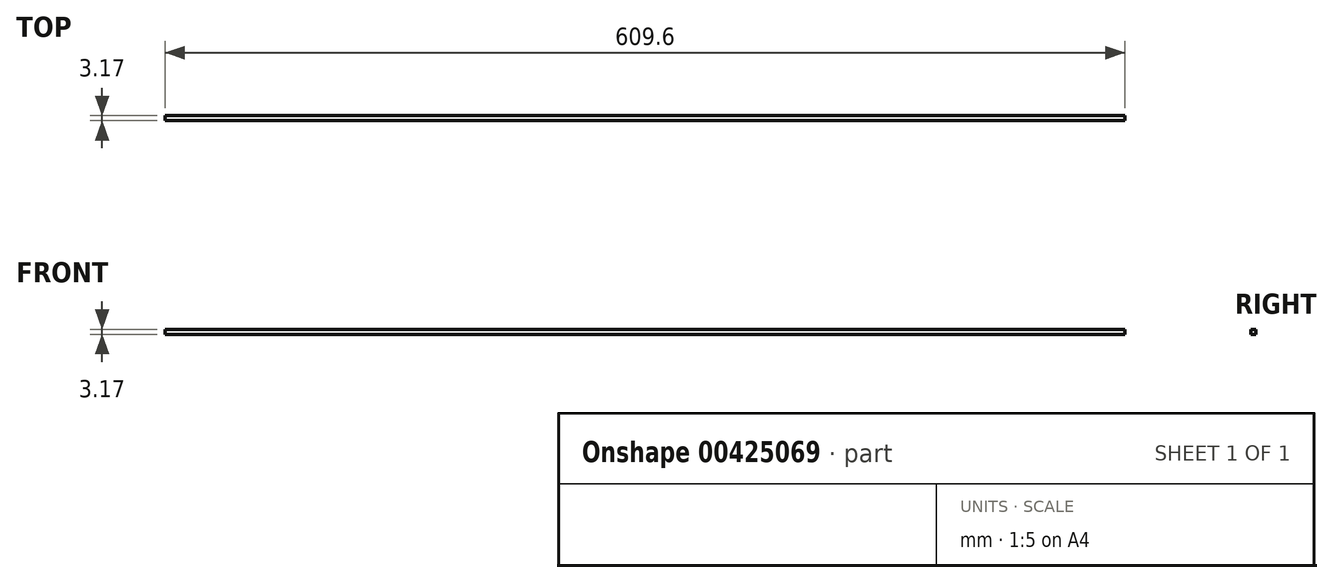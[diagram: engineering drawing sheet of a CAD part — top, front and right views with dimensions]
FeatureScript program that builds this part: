
annotation { "Feature Type Name" : "Feature", "Feature Type Description" : "" }
export const myFeature = defineFeature(function(context is Context, id is Id, definition is map)
    precondition{}
    {
        {
            var Q0;
            Q0=qCreatedBy(makeId("Front.planeOp"),FACE);
            var sketch = newSketch(context, id + "F0", { "sketchPlane" : qUnion([Q0])});
            skLineSegment(sketch, "E0", {"start": v(-305.5, 35.04) * mm, "end": v(304.1, 35.04) * mm});
            skLineSegment(sketch, "E1", {"start": v(304.1, 35.04) * mm, "end": v(304.1, 31.87) * mm});
            skLineSegment(sketch, "E2", {"start": v(304.1, 31.87) * mm, "end": v(-305.5, 31.87) * mm});
            skLineSegment(sketch, "E3", {"start": v(-305.5, 31.87) * mm, "end": v(-305.5, 35.04) * mm});
            skSolve(sketch);
        }
        {
            var Q0;
            Q0=makeQuery(id+"F0.imprint","IMPRINT",FACE,{"disambiguationData":[TD([[makeQuery(id+"F0.imprint","IMPRINT",EDGE,{"derivedFrom":sQuery(id+"F0.wireOp",EDGE,"E0")}),-1.0]])]});
            extrude(context, id + "F1", {"entities" : qUnion([Q0]), "depth" : 3.17 * mm});
        }
    });
